# Revit family: 2CKA006401A0048
name_source: partatom
category: Elektroinstallationen
revit_build: Autodesk Revit 2017 (Build: 20160225_1515(x64)
units: mm (PartAtom-declared; Revit-internal decimal feet)

## family parameters
Basisbauteil = Fläche
Beim Laden mit Abzugskörper schneiden = Nein
Bemaßung runder Anschluss = Durchmesser verwenden
Beschriftungsausrichtung beibehalten = Nein
Gemeinsam genutzt = Nein
Raumberechnungspunkt = Nein
Teiletyp = Normal

## types (1)
- 2CKA006401A0048
    Ausführung = Relais
    Ausführung der Oberfläche = glänzend
    BIM = https://media.live.bim.site
    BIMSITE_PRODUCT_ID = 80ec8b6eb32c0b88f7ff0830991e87816e59eee8
    Befestigungsart = Krallen-/Schraubbefestigung
    Bemessungsstrom = 10 A
    Beschreibung = Busch-Universal-Relais-Einsatz, UP-Montagedosen und -Einsätze, Einsätze für Bewegungsmelder/Komfortschalter, Busch-Universal-Relais-Einsatz 3-Leiter-Anschlusstechnik (Neutralleiter erforderlich). Für Busch-Wächter 180 UP Sensor Standard 6810-21x-101. Für Busch-Wächter 180 UP Sensor Komfort II 6800-xxx-104 und 6800-xxx-104M. Für Busch-Wächter 180 UP Sensor für Allwetter 44 6800-3x-102C. Für Busch-Wächter Präsenz tech 6813-xxx-101 und 6813/11-xxx. Für Komfort-Timer-Bedienelement 6455-101. Für Busch-Ferncontrol IR Bedienelement 6067-xxx-10x. Für Bedienelement mit Glimmlampe 6543-xxx-10x. Kombinierbar mit Busch-Wächter Nebenstellen-Einsatz 6805 U. Bedienung auch über konventionelle Taster (2020 US, 2021/6 UK) möglich. Nennspannung: , +10 % / -10 % Nennfrequenz: 50 Hz Ausgänge: 1x Schließer, potenzialgebunden Lastart: 230 V-Glühlampen, 230 V-Halogenlampen, Leuchtstofflampen und Niedervolt Halogenlampen, die über Transformatoren betrieben werden. Nennstrom: 10 AX Nennleistung: 2300 W/VA Temperaturbereich Gerät: -25 °C bis 55 °C 60669-2-1
    Datenblatt = https://media.live.bim.site BJE_DinA4-Online-ger.pdf
    Datenblatt 1 = https://media.live.bim.site BJE_DinA4-Online-dut.pdf
    Datenblatt 2 = https://media.live.bim.site U-102_CE_XX_V01_2CKA100000E1566.pdf
    Datenblatt 3 = https://media.live.bim.site
    Farbe = schwarz
    Frequenz [Hz] = [50:50]
    GTIN = 4011395991299
    HAN = 2CKA006401A0048
    HeinzeBIM = https://www.heinze.de
    Hersteller = Busch-Jaeger
    Ist System = Nein
    Ist Zubehör = Nein
    Lastart = universal und LED Retrofit
    Montageart = Unterputz
    Nebenstelleneingang = Ja
    Nennspannung [V] [Volt] = 230
    Oberfläche = unbehandelt
    Schaltleistung [Voltampere] = [0:2300]
    TYPE = 6401 U-102
    Typname = Busch-Universal-Relais-Einsatz, UP-Montagedosen und -Einsätze, Einsätze für Bewegungsmelder/Komfortschalter
    URL = https://www.busch-jaeger.de
    Verwendbar mit Bewegungsmelder = Ja
    Verwendbar mit IR-Taste = Ja
    Verwendbar mit Präsenzmelder = Ja
    Verwendbar mit Taste = Ja
    Verwendbar mit Zeitschalter/Timer = Ja
    Vorgabe-Ansicht = 1219 mm
    Werkstoff = Kunststoff
    White = White
    Zusammenstellung = Basiselement

## geometry (parser evidence)
native form markers: Sweep x3
no freeform markers — native parametric forms only
